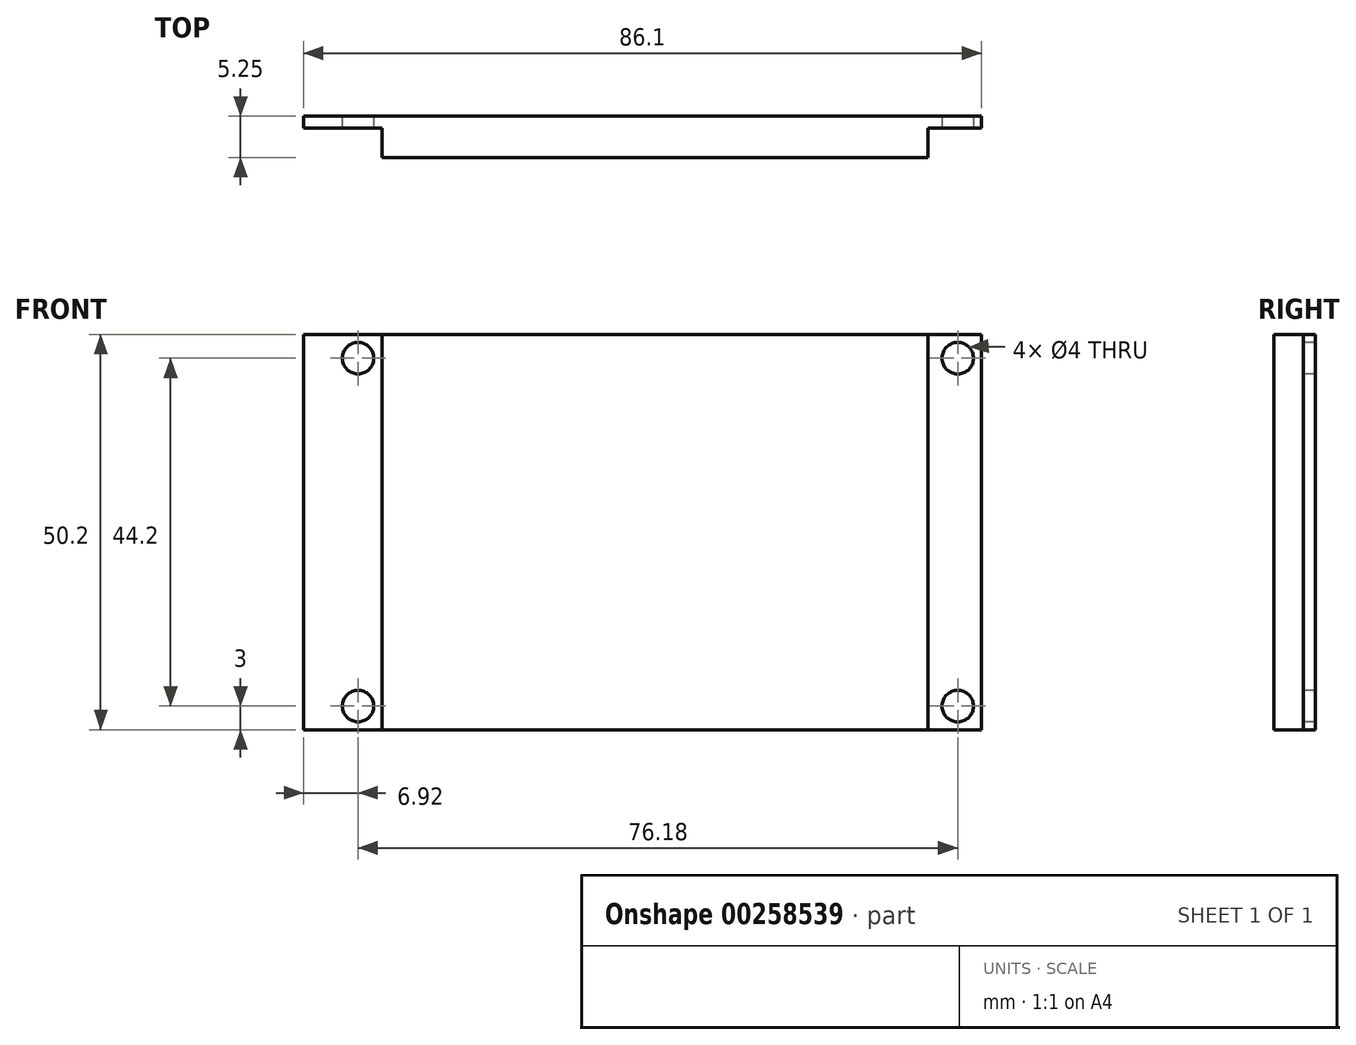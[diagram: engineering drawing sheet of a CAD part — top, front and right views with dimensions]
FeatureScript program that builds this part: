
annotation { "Feature Type Name" : "Feature", "Feature Type Description" : "" }
export const myFeature = defineFeature(function(context is Context, id is Id, definition is map)
    precondition{}
    {
        {
            var Q0;
            Q0=qCreatedBy(makeId("Front.planeOp"),FACE);
            var sketch = newSketch(context, id + "F0", { "sketchPlane" : qUnion([Q0])});
            skLineSegment(sketch, "E0.bottom", {"start": v(-43.05, 25.1) * mm, "end": v(43.05, 25.1) * mm});
            skLineSegment(sketch, "E0.top", {"start": v(-43.05, -25.1) * mm, "end": v(43.05, -25.1) * mm});
            skLineSegment(sketch, "E0.left", {"start": v(-43.05, 25.1) * mm, "end": v(-43.05, -25.1) * mm});
            skLineSegment(sketch, "E0.right", {"start": v(43.05, 25.1) * mm, "end": v(43.05, -25.1) * mm});
            skPoint(sketch, "E0.middle", {"position": v(0, 0) * mm});
            skSolve(sketch);
        }
        {
            var Q0;
            Q0 = qSketchRegion(id + "F0", true);
            extrude(context, id + "F1", {"entities" : qUnion([Q0]), "oppositeDirection" : true, "depth" : 1.5 * mm});
        }
        {
            var Q0;
            Q0=qCreatedBy(makeId("Front.planeOp"),FACE);
            var sketch = newSketch(context, id + "F2", { "sketchPlane" : qUnion([Q0])});
            skLineSegment(sketch, "E1.bottom", {"start": v(-33.05, 25.1) * mm, "end": v(36.25, 25.1) * mm});
            skLineSegment(sketch, "E1.top", {"start": v(-33.05, -25.1) * mm, "end": v(36.25, -25.1) * mm});
            skLineSegment(sketch, "E1.left", {"start": v(-33.05, 25.1) * mm, "end": v(-33.05, -25.1) * mm});
            skLineSegment(sketch, "E1.right", {"start": v(36.25, 25.1) * mm, "end": v(36.25, -25.1) * mm});
            skSolve(sketch);
        }
        {
            var Q0;
            Q0 = qSketchRegion(id + "F2", true);
            extrude(context, id + "F3", {"entities" : qUnion([Q0]), "operationType" : NewBodyOperationType.ADD, "depth" : 3.75 * mm});
        }
        {
            var Q0;
            Q0=qCreatedBy(makeId("Front.planeOp"),FACE);
            var sketch = newSketch(context, id + "F4", { "sketchPlane" : qUnion([Q0])});
            skCircle(sketch, "E2", {"center": v(-36.13, 22.1) * mm, "radius": 2 * mm});
            skCircle(sketch, "E3", {"center": v(-36.13, -22.1) * mm, "radius": 2 * mm});
            skCircle(sketch, "E4", {"center": v(40.05, 22.1) * mm, "radius": 2 * mm});
            skCircle(sketch, "E5", {"center": v(40.05, -22.1) * mm, "radius": 2 * mm});
            skSolve(sketch);
        }
        {
            var Q0;
            Q0 = qSketchRegion(id + "F4", true);
            extrude(context, id + "F5", {"entities" : qUnion([Q0]), "operationType" : NewBodyOperationType.REMOVE, "endBound" : BoundingType.THROUGH_ALL, "oppositeDirection" : true, "depth" : 25 * mm});
        }
    });
